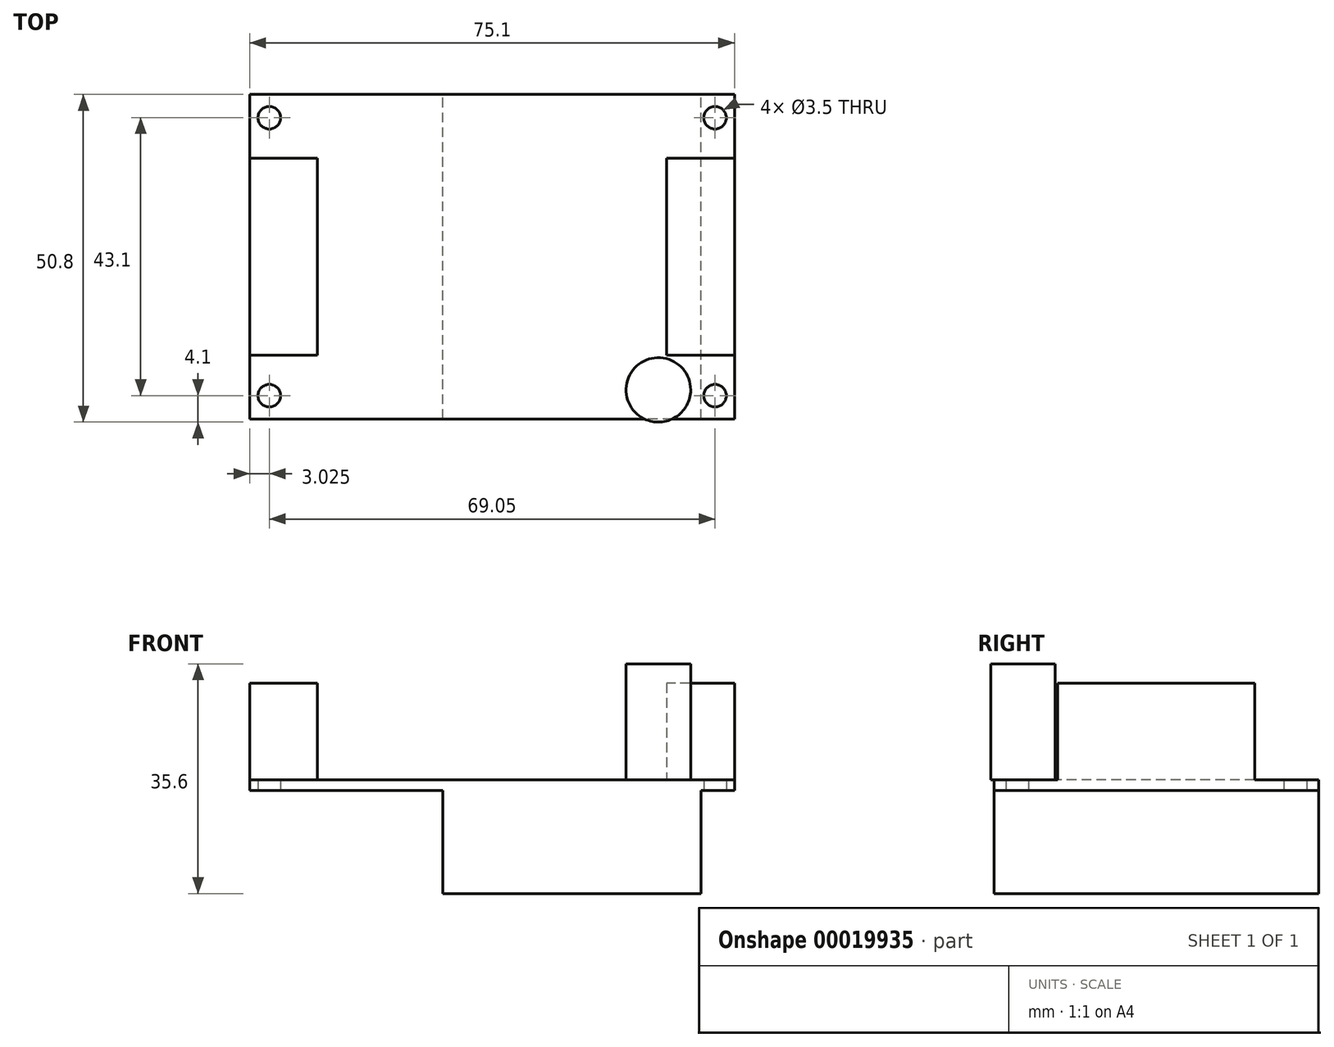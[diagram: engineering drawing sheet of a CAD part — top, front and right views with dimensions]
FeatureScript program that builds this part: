
annotation { "Feature Type Name" : "Feature", "Feature Type Description" : "" }
export const myFeature = defineFeature(function(context is Context, id is Id, definition is map)
    precondition{}
    {
        {
            var Q0;
            Q0=qCreatedBy(makeId("Top.planeOp"),FACE);
            var sketch = newSketch(context, id + "F0", { "sketchPlane" : qUnion([Q0])});
            skLineSegment(sketch, "E0.rect.bottom", {"start": v(37.55, -25.15) * mm, "end": v(-37.55, -25.15) * mm});
            skLineSegment(sketch, "E0.rect.top", {"start": v(37.55, 25.15) * mm, "end": v(-37.55, 25.15) * mm});
            skLineSegment(sketch, "E0.rect.left", {"start": v(37.55, -25.15) * mm, "end": v(37.55, 25.15) * mm});
            skLineSegment(sketch, "E0.rect.right", {"start": v(-37.55, -25.15) * mm, "end": v(-37.55, 25.15) * mm});
            skPoint(sketch, "E0.rect.middle", {"position": v(0, 0) * mm});
            skCircle(sketch, "E1", {"center": v(-34.53, 21.55) * mm, "radius": 1.75 * mm});
            skCircle(sketch, "E2", {"center": v(-34.53, -21.55) * mm, "radius": 1.75 * mm});
            skCircle(sketch, "E3", {"center": v(34.52, -21.55) * mm, "radius": 1.75 * mm});
            skCircle(sketch, "E4", {"center": v(34.52, 21.55) * mm, "radius": 1.75 * mm});
            skLineSegment(sketch, "E5", {"start": v(-34.52, 21.55) * mm, "end": v(-37.55, 0) * mm, "construction": true});
            skLineSegment(sketch, "E6", {"start": v(-37.55, 0) * mm, "end": v(-34.52, -21.55) * mm, "construction": true});
            skLineSegment(sketch, "E7", {"start": v(-34.53, 21.55) * mm, "end": v(0, 25.15) * mm, "construction": true});
            skLineSegment(sketch, "E8", {"start": v(0, 25.15) * mm, "end": v(34.52, 21.55) * mm, "construction": true});
            skSolve(sketch);
        }
        {
            var Q0;
            Q0 = qSketchRegion(id + "F0", true);
            extrude(context, id + "F1", {"entities" : qUnion([Q0]), "depth" : 1.6 * mm});
        }
        {
            var Q0;
            Q0=makeQuery(id+"F1.opExtrude","CAP_FACE",FACE,{"disambiguationData":[OSD([sQuery(id+"F0.wireOp",EDGE,"E0.rect.bottom"),sQuery(id+"F0.wireOp",EDGE,"E0.rect.top"),sQuery(id+"F0.wireOp",EDGE,"E0.rect.left"),sQuery(id+"F0.wireOp",EDGE,"E0.rect.right"),sQuery(id+"F0.wireOp",EDGE,"E1"),sQuery(id+"F0.wireOp",EDGE,"E2"),sQuery(id+"F0.wireOp",EDGE,"E3"),sQuery(id+"F0.wireOp",EDGE,"E4")])],"isStart":false});
            var sketch = newSketch(context, id + "F2", { "sketchPlane" : qUnion([Q0])});
            skLineSegment(sketch, "E9.bottom", {"start": v(-37.55, 15.25) * mm, "end": v(-27.05, 15.25) * mm});
            skLineSegment(sketch, "E9.top", {"start": v(-37.55, -15.25) * mm, "end": v(-27.05, -15.25) * mm});
            skLineSegment(sketch, "E9.left", {"start": v(-37.55, 15.25) * mm, "end": v(-37.55, -15.25) * mm});
            skLineSegment(sketch, "E9.right", {"start": v(-27.05, 15.25) * mm, "end": v(-27.05, -15.25) * mm});
            skLineSegment(sketch, "E10.bottom", {"start": v(37.55, 15.25) * mm, "end": v(27.05, 15.25) * mm});
            skLineSegment(sketch, "E10.top", {"start": v(37.55, -15.25) * mm, "end": v(27.05, -15.25) * mm});
            skLineSegment(sketch, "E10.left", {"start": v(37.55, 15.25) * mm, "end": v(37.55, -15.25) * mm});
            skLineSegment(sketch, "E10.right", {"start": v(27.05, 15.25) * mm, "end": v(27.05, -15.25) * mm});
            skLineSegment(sketch, "E11", {"start": v(-27.05, 15.25) * mm, "end": v(-37.55, 25.15) * mm, "construction": true});
            skLineSegment(sketch, "E12", {"start": v(-27.05, -15.25) * mm, "end": v(-37.55, -25.15) * mm, "construction": true});
            skLineSegment(sketch, "E13", {"start": v(27.05, -15.25) * mm, "end": v(37.55, -25.15) * mm, "construction": true});
            skLineSegment(sketch, "E14", {"start": v(27.05, 15.25) * mm, "end": v(37.55, 25.15) * mm, "construction": true});
            skSolve(sketch);
        }
        {
            var Q0;
            Q0 = qSketchRegion(id + "F2", true);
            extrude(context, id + "F3", {"entities" : qUnion([Q0]), "operationType" : NewBodyOperationType.ADD, "depth" : 15 * mm});
        }
        {
            var Q0;
            Q0=makeQuery(id+"F1.opExtrude","CAP_FACE",FACE,{"disambiguationData":[OSD([sQuery(id+"F0.wireOp",EDGE,"E0.rect.bottom"),sQuery(id+"F0.wireOp",EDGE,"E0.rect.top"),sQuery(id+"F0.wireOp",EDGE,"E0.rect.left"),sQuery(id+"F0.wireOp",EDGE,"E0.rect.right"),sQuery(id+"F0.wireOp",EDGE,"E1"),sQuery(id+"F0.wireOp",EDGE,"E2"),sQuery(id+"F0.wireOp",EDGE,"E3"),sQuery(id+"F0.wireOp",EDGE,"E4")])],"isStart":true});
            var sketch = newSketch(context, id + "F4", { "sketchPlane" : qUnion([Q0])});
            skLineSegment(sketch, "E15.bottom", {"start": v(-7.65, 25.15) * mm, "end": v(32.35, 25.15) * mm});
            skLineSegment(sketch, "E15.top", {"start": v(-7.65, -25.15) * mm, "end": v(32.35, -25.15) * mm});
            skLineSegment(sketch, "E15.left", {"start": v(-7.65, 25.15) * mm, "end": v(-7.65, -25.15) * mm});
            skLineSegment(sketch, "E15.right", {"start": v(32.35, 25.15) * mm, "end": v(32.35, -25.15) * mm});
            skSolve(sketch);
        }
        {
            var Q0;
            Q0 = qSketchRegion(id + "F4", true);
            extrude(context, id + "F5", {"entities" : qUnion([Q0]), "operationType" : NewBodyOperationType.ADD, "depth" : 16 * mm});
        }
        {
            var Q0;
            Q0=makeQuery(id+"F1.opExtrude","CAP_FACE",FACE,{"disambiguationData":[OSD([sQuery(id+"F0.wireOp",EDGE,"E0.rect.bottom"),sQuery(id+"F0.wireOp",EDGE,"E0.rect.top"),sQuery(id+"F0.wireOp",EDGE,"E0.rect.left"),sQuery(id+"F0.wireOp",EDGE,"E0.rect.right"),sQuery(id+"F0.wireOp",EDGE,"E1"),sQuery(id+"F0.wireOp",EDGE,"E2"),sQuery(id+"F0.wireOp",EDGE,"E3"),sQuery(id+"F0.wireOp",EDGE,"E4")])],"isStart":false});
            var sketch = newSketch(context, id + "F6", { "sketchPlane" : qUnion([Q0])});
            skCircle(sketch, "E16", {"center": v(25.75, -20.65) * mm, "radius": 5 * mm});
            skSolve(sketch);
        }
        {
            var Q0;
            Q0 = qSketchRegion(id + "F6", true);
            extrude(context, id + "F7", {"entities" : qUnion([Q0]), "operationType" : NewBodyOperationType.ADD, "depth" : 18 * mm});
        }
    });
